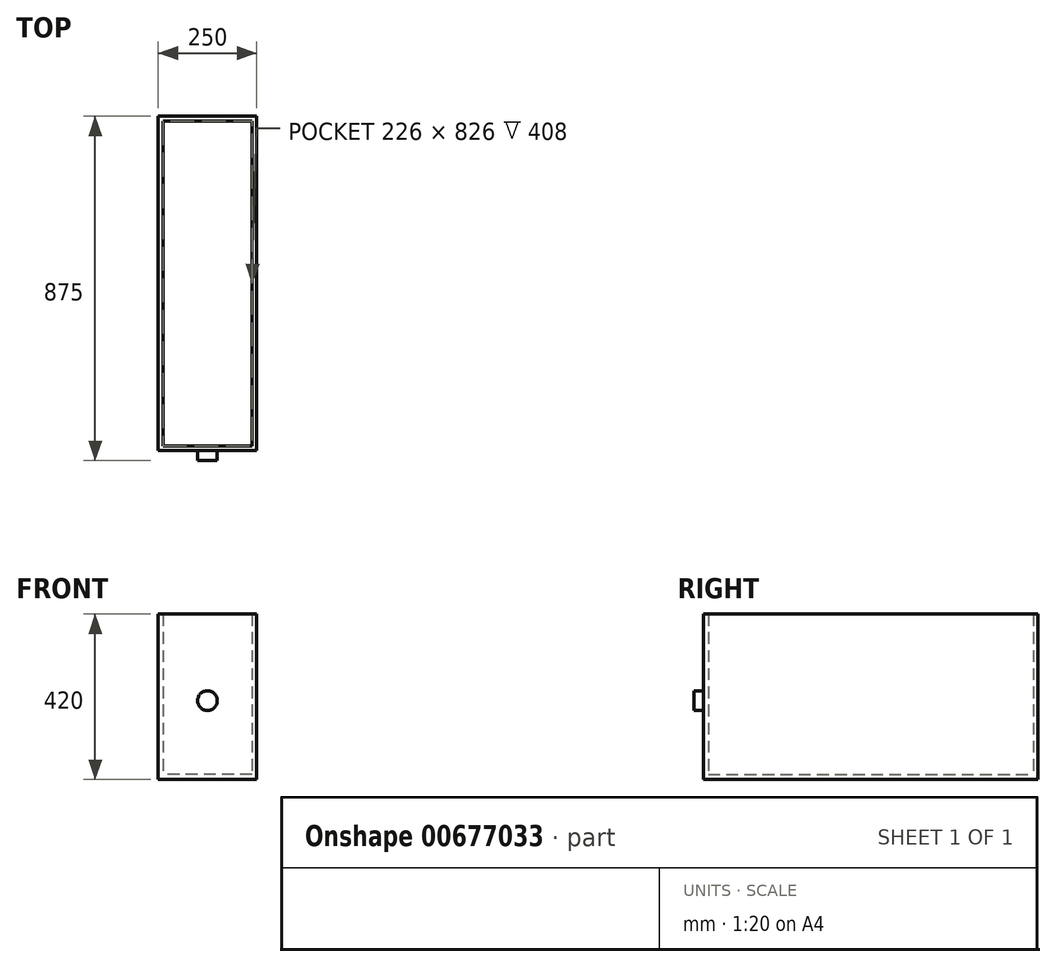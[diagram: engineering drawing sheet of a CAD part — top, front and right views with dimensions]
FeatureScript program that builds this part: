
annotation { "Feature Type Name" : "Feature", "Feature Type Description" : "" }
export const myFeature = defineFeature(function(context is Context, id is Id, definition is map)
    precondition{}
    {
        {
            var Q0;
            Q0=qCreatedBy(makeId("Top.planeOp"),FACE);
            var sketch = newSketch(context, id + "F0", { "sketchPlane" : qUnion([Q0])});
            skLineSegment(sketch, "E0.bottom", {"start": v(0, 0) * mm, "end": v(250, 0) * mm});
            skLineSegment(sketch, "E0.top", {"start": v(0, -850) * mm, "end": v(250, -850) * mm});
            skLineSegment(sketch, "E0.left", {"start": v(0, 0) * mm, "end": v(0, -850) * mm});
            skLineSegment(sketch, "E0.right", {"start": v(250, 0) * mm, "end": v(250, -850) * mm});
            skSolve(sketch);
        }
        {
            var Q0;
            Q0=makeQuery(id+"F0.imprint","IMPRINT",FACE,{"disambiguationData":[TD([[makeQuery(id+"F0.imprint","IMPRINT",EDGE,{"derivedFrom":sQuery(id+"F0.wireOp",EDGE,"E0.bottom")}),-1.0]])]});
            extrude(context, id + "F1", {"entities" : qUnion([Q0]), "depth" : 12 * mm, "offsetDistance" : 25 * mm});
        }
        {
            var Q0;
            Q0=makeQuery(id+"F1.opExtrude","CAP_FACE",FACE,{"disambiguationData":[OSD([sQuery(id+"F0.wireOp",EDGE,"E0.bottom"),sQuery(id+"F0.wireOp",EDGE,"E0.top"),sQuery(id+"F0.wireOp",EDGE,"E0.left"),sQuery(id+"F0.wireOp",EDGE,"E0.right")])],"isStart":false});
            var sketch = newSketch(context, id + "F2", { "sketchPlane" : qUnion([Q0])});
            skLineSegment(sketch, "E1.bottom", {"start": v(250, -850) * mm, "end": v(0, -850) * mm});
            skLineSegment(sketch, "E1.top", {"start": v(250, 0) * mm, "end": v(0, 0) * mm});
            skLineSegment(sketch, "E1.left", {"start": v(250, -850) * mm, "end": v(250, 0) * mm});
            skLineSegment(sketch, "E1.right", {"start": v(0, -850) * mm, "end": v(0, 0) * mm});
            skLineSegment(sketch, "E2.0", {"start": v(12, -838) * mm, "end": v(12, -12) * mm});
            skLineSegment(sketch, "E2.1", {"start": v(238, -838) * mm, "end": v(12, -838) * mm});
            skLineSegment(sketch, "E2.2", {"start": v(238, -838) * mm, "end": v(238, -12) * mm});
            skLineSegment(sketch, "E2.3", {"start": v(238, -12) * mm, "end": v(12, -12) * mm});
            skSolve(sketch);
        }
        {
            var Q0;
            Q0 = qSketchRegion(id + "F2", true);
            extrude(context, id + "F3", {"entities" : qUnion([Q0]), "operationType" : NewBodyOperationType.ADD, "depth" : 408 * mm, "offsetDistance" : 25 * mm});
        }
        {
            var Q0;
            Q0=makeQuery(id+"F3.boolean.opBoolean","MERGE",FACE,{"derivedFrom":[makeQuery(id+"F1.opExtrude","SWEPT_FACE",FACE,{"disambiguationData":[OSD([sQuery(id+"F0.wireOp",EDGE,"E0.top")])]}),makeQuery(id+"F3.opExtrude","SWEPT_FACE",FACE,{"disambiguationData":[OSD([sQuery(id+"F2.wireOp",EDGE,"E1.bottom")])]})]});
            var sketch = newSketch(context, id + "F4", { "sketchPlane" : qUnion([Q0])});
            skCircle(sketch, "E3", {"center": v(125, 200) * mm, "radius": 25 * mm});
            skSolve(sketch);
        }
        {
            var Q0;
            Q0=makeQuery(id+"F4.imprint","IMPRINT",FACE,{"disambiguationData":[TD([[makeQuery(id+"F4.imprint","IMPRINT",EDGE,{"derivedFrom":sQuery(id+"F4.wireOp",EDGE,"E3")}),1.0]])]});
            extrude(context, id + "F5", {"entities" : qUnion([Q0]), "operationType" : NewBodyOperationType.ADD, "depth" : 25 * mm, "offsetDistance" : 25 * mm});
        }
    });
